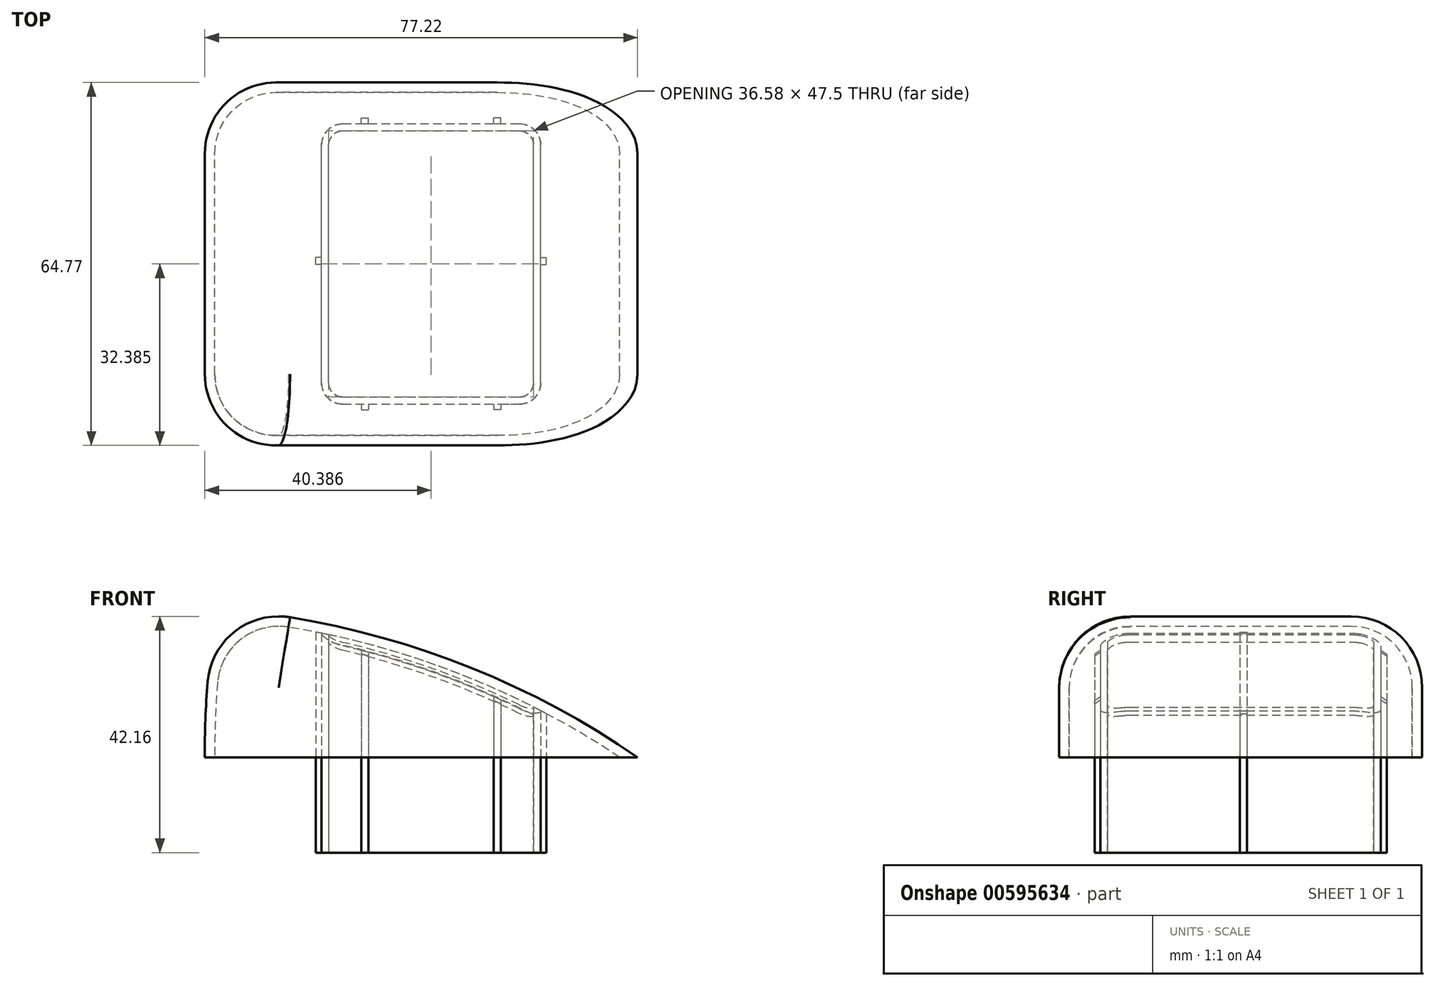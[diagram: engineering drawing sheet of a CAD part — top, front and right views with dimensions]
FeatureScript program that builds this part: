
annotation { "Feature Type Name" : "Feature", "Feature Type Description" : "" }
export const myFeature = defineFeature(function(context is Context, id is Id, definition is map)
    precondition{}
    {
        {
            var Q0;
            Q0=qCreatedBy(makeId("Front.planeOp"),FACE);
            var sketch = newSketch(context, id + "F0", { "sketchPlane" : qUnion([Q0])});
            skLineSegment(sketch, "E0", {"start": v(0, 0) * mm, "end": v(77.22, 0) * mm});
            skArc(sketch, "E1", {"start": v(77.22, 0) * mm, "mid": v(46.3, 16.45) * mm, "end": v(12.45, 25.4) * mm});
            skArc(sketch, "E2", {"start": v(0.76, 16.26) * mm, "mid": v(0.16, 8.14) * mm, "end": v(0, 0) * mm});
            skArc(sketch, "E3", {"start": v(12.45, 25.4) * mm, "mid": v(5.03, 22.84) * mm, "end": v(0.76, 16.26) * mm});
            skSolve(sketch);
        }
        {
            var Q0;
            Q0=makeQuery(id+"F0.imprint","IMPRINT",FACE,{"disambiguationData":[TD([[makeQuery(id+"F0.imprint","IMPRINT",EDGE,{"derivedFrom":sQuery(id+"F0.wireOp",EDGE,"E0")}),1.0]])]});
            extrude(context, id + "F1", {"entities" : qUnion([Q0]), "depth" : 64.77 * mm, "offsetDistance" : 25.4 * mm});
        }
        {
            var Q0;
            Q0=makeQuery(id+"F1.opExtrude","CAP_EDGE",EDGE,{"disambiguationData":[OSD([sQuery(id+"F0.wireOp",EDGE,"E1")])],"isStart":false});
            var Q1;
            Q1=makeQuery(id+"F1.opExtrude","CAP_EDGE",EDGE,{"disambiguationData":[OSD([sQuery(id+"F0.wireOp",EDGE,"E2")])],"isStart":true});
            fillet(context, id + "F2", {"entities" : qUnion([Q0, Q1]), "radius" : 12.7 * mm, "tangentPropagation" : true, "allowEdgeOverflow" : false});
        }
        {
            var Q0;
            Q0=makeQuery(id+"F2.opFillet","BLEND_EDGE",EDGE,{"blendedFrom":[makeQuery(id+"F1.opExtrude","CAP_EDGE",EDGE,{"disambiguationData":[OSD([sQuery(id+"F0.wireOp",EDGE,"E2")])],"isStart":true}),makeQuery(id+"F1.opExtrude","SWEPT_FACE",FACE,{"disambiguationData":[OSD([sQuery(id+"F0.wireOp",EDGE,"E3")])]})],"blendedInto":[makeQuery(id+"F1.opExtrude","SWEPT_FACE",FACE,{"disambiguationData":[OSD([sQuery(id+"F0.wireOp",EDGE,"E3")])]})]});
            var Q1;
            Q1=makeQuery(id+"F1.opExtrude","CAP_EDGE",EDGE,{"disambiguationData":[OSD([sQuery(id+"F0.wireOp",EDGE,"E1")])],"isStart":true});
            fillet(context, id + "F3", {"entities" : qUnion([Q0, Q1]), "radius" : 12.7 * mm, "tangentPropagation" : true, "allowEdgeOverflow" : false});
        }
        {
            var Q0;
            Q0=makeQuery(id+"F3.opFillet","BLEND_EDGE",EDGE,{"blendedFrom":[makeQuery(id+"F1.opExtrude","SWEPT_EDGE",EDGE,{"disambiguationData":[OSD([sQuery(id+"F0.wireOp",EDGE,"E2"),sQuery(id+"F0.wireOp",EDGE,"E3")])]}),makeQuery(id+"F2.opFillet","BLEND_FACE",FACE,{"disambiguationData":[OSD([sQuery(id+"F0.wireOp",EDGE,"E1")])]})],"blendedInto":[makeQuery(id+"F2.opFillet","BLEND_FACE",FACE,{"disambiguationData":[OSD([sQuery(id+"F0.wireOp",EDGE,"E1")])]})]});
            fillet(context, id + "F4", {"entities" : qUnion([Q0]), "radius" : 12.7 * mm, "tangentPropagation" : true, "allowEdgeOverflow" : false});
        }
        {
            var Q0;
            Q0=makeQuery(id+"F1.opExtrude","SWEPT_FACE",FACE,{"disambiguationData":[OSD([sQuery(id+"F0.wireOp",EDGE,"E0")])]});
            shell(context, id + "F5", {"entities" : qUnion([Q0]), "thickness" : 1.78 * mm});
        }
        {
            var Q0;
            Q0=makeQuery(id+"F1.opExtrude","SWEPT_FACE",FACE,{"disambiguationData":[OSD([sQuery(id+"F0.wireOp",EDGE,"E0")])]});
            cPlane(context, id + "F6", {"entities" : qUnion([Q0]), "cplaneType" : CPlaneType.OFFSET, "offset" : 0 * mm, "width" : 152.4 * mm, "height" : 152.4 * mm});
        }
        {
            var Q0;
            Q0=qCreatedBy(id+"F6.planeOp",FACE);
            var sketch = newSketch(context, id + "F7", { "sketchPlane" : qUnion([Q0])});
            skLineSegment(sketch, "E4.bottom", {"start": v(24.64, 57.4) * mm, "end": v(56.13, 57.4) * mm});
            skLineSegment(sketch, "E4.top", {"start": v(24.64, 7.37) * mm, "end": v(56.13, 7.37) * mm});
            skLineSegment(sketch, "E4.left", {"start": v(20.83, 53.6) * mm, "end": v(20.83, 11.18) * mm});
            skLineSegment(sketch, "E4.right", {"start": v(59.94, 53.6) * mm, "end": v(59.94, 11.18) * mm});
            skPoint(sketch, "E5.visualSharp", {"position": v(20.83, 57.4) * mm});
            skArc(sketch, "E5.filletArc", {"start": v(24.64, 57.4) * mm, "mid": v(21.94, 56.29) * mm, "end": v(20.83, 53.6) * mm});
            skPoint(sketch, "E6.visualSharp", {"position": v(20.83, 7.37) * mm});
            skArc(sketch, "E6.filletArc", {"start": v(20.83, 11.18) * mm, "mid": v(21.94, 8.48) * mm, "end": v(24.64, 7.37) * mm});
            skPoint(sketch, "E7.visualSharp", {"position": v(59.94, 7.37) * mm});
            skArc(sketch, "E7.filletArc", {"start": v(56.13, 7.37) * mm, "mid": v(58.83, 8.48) * mm, "end": v(59.94, 11.18) * mm});
            skPoint(sketch, "E8.visualSharp", {"position": v(59.94, 57.4) * mm});
            skArc(sketch, "E8.filletArc", {"start": v(59.94, 53.6) * mm, "mid": v(58.83, 56.29) * mm, "end": v(56.13, 57.4) * mm});
            skSolve(sketch);
        }
        {
            var Q0;
            Q0=makeQuery(id+"F7.imprint","IMPRINT",FACE,{"disambiguationData":[TD([[makeQuery(id+"F7.imprint","IMPRINT",EDGE,{"derivedFrom":sQuery(id+"F7.wireOp",EDGE,"E4.bottom")}),-1.0]])]});
            extrude(context, id + "F8", {"entities" : qUnion([Q0]), "endBound" : BoundingType.UP_TO_NEXT, "oppositeDirection" : true, "depth" : 25.4 * mm, "offsetDistance" : 25.4 * mm});
        }
        {
            var Q0;
            Q0=makeQuery(id+"F8.opExtrude","CAP_FACE",FACE,{"disambiguationData":[OSD([sQuery(id+"F7.wireOp",EDGE,"E4.bottom"),sQuery(id+"F7.wireOp",EDGE,"E4.top"),sQuery(id+"F7.wireOp",EDGE,"E4.left"),sQuery(id+"F7.wireOp",EDGE,"E4.right"),sQuery(id+"F7.wireOp",EDGE,"E5.filletArc"),sQuery(id+"F7.wireOp",EDGE,"E6.filletArc"),sQuery(id+"F7.wireOp",EDGE,"E7.filletArc"),sQuery(id+"F7.wireOp",EDGE,"E8.filletArc")])],"isStart":true});
            extrude(context, id + "F9", {"entities" : qUnion([Q0]), "operationType" : NewBodyOperationType.ADD, "depth" : 17.02 * mm, "offsetDistance" : 25.4 * mm});
        }
        {
            var Q0;
            Q0=makeQuery(id+"F9.opExtrude","CAP_FACE",FACE,{"disambiguationData":[OSD([sQuery(id+"F7.wireOp",EDGE,"E4.bottom"),sQuery(id+"F7.wireOp",EDGE,"E4.top"),sQuery(id+"F7.wireOp",EDGE,"E4.left"),sQuery(id+"F7.wireOp",EDGE,"E4.right"),sQuery(id+"F7.wireOp",EDGE,"E5.filletArc"),sQuery(id+"F7.wireOp",EDGE,"E6.filletArc"),sQuery(id+"F7.wireOp",EDGE,"E7.filletArc"),sQuery(id+"F7.wireOp",EDGE,"E8.filletArc")])],"isStart":false});
            shell(context, id + "F10", {"entities" : qUnion([Q0]), "thickness" : 1.27 * mm});
        }
        {
            var Q0;
            Q0=makeQuery(id+"F9.opExtrude","CAP_FACE",FACE,{"disambiguationData":[OSD([sQuery(id+"F7.wireOp",EDGE,"E4.bottom"),sQuery(id+"F7.wireOp",EDGE,"E4.top"),sQuery(id+"F7.wireOp",EDGE,"E4.left"),sQuery(id+"F7.wireOp",EDGE,"E4.right"),sQuery(id+"F7.wireOp",EDGE,"E5.filletArc"),sQuery(id+"F7.wireOp",EDGE,"E6.filletArc"),sQuery(id+"F7.wireOp",EDGE,"E7.filletArc"),sQuery(id+"F7.wireOp",EDGE,"E8.filletArc")])],"isStart":false});
            var sketch = newSketch(context, id + "F11", { "sketchPlane" : qUnion([Q0])});
            skLineSegment(sketch, "E9", {"start": v(20.83, 57.4) * mm, "end": v(27.94, 57.4) * mm});
            skLineSegment(sketch, "E10.bottom", {"start": v(27.94, 57.4) * mm, "end": v(29.22, 57.4) * mm});
            skLineSegment(sketch, "E10.top", {"start": v(27.94, 58.42) * mm, "end": v(29.22, 58.42) * mm});
            skLineSegment(sketch, "E10.left", {"start": v(27.94, 57.4) * mm, "end": v(27.94, 58.42) * mm});
            skLineSegment(sketch, "E10.right", {"start": v(29.22, 57.4) * mm, "end": v(29.22, 58.42) * mm});
            skLineSegment(sketch, "E11", {"start": v(59.94, 57.4) * mm, "end": v(52.84, 57.4) * mm});
            skLineSegment(sketch, "E12.bottom", {"start": v(52.84, 57.4) * mm, "end": v(51.58, 57.4) * mm});
            skLineSegment(sketch, "E12.top", {"start": v(52.84, 58.42) * mm, "end": v(51.58, 58.42) * mm});
            skLineSegment(sketch, "E12.left", {"start": v(52.84, 57.4) * mm, "end": v(52.84, 58.42) * mm});
            skLineSegment(sketch, "E12.right", {"start": v(51.58, 57.4) * mm, "end": v(51.58, 58.42) * mm});
            skSolve(sketch);
        }
        {
            var Q0;
            Q0=makeQuery(id+"F11.imprint","IMPRINT",FACE,{"disambiguationData":[TD([[makeQuery(id+"F11.imprint","IMPRINT",EDGE,{"derivedFrom":sQuery(id+"F11.wireOp",EDGE,"E12.bottom")}),1.0]])]});
            var Q1;
            {var subQ4=sQuery(id+"F11.wireOp",EDGE,"E10.bottom");Q1=makeQuery(id+"F11.imprint","IMPRINT",FACE,{"disambiguationData":[TD([[makeQuery(id+"F11.imprint","IMPRINT",EDGE,{"derivedFrom":subQ4}),-1.0]])]});}
            var Q2;
            Q2=makeQuery(id+"F11.imprint","IMPRINT",FACE,{"disambiguationData":[TD([[makeQuery(id+"F11.imprint","IMPRINT",EDGE,{"derivedFrom":sQuery(id+"F11.wireOp",EDGE,"E10.bottom")}),1.0]])]});
            extrude(context, id + "F12", {"entities" : qUnion([Q0, Q1, Q2]), "endBound" : BoundingType.UP_TO_NEXT, "oppositeDirection" : true, "depth" : 25.4 * mm, "offsetDistance" : 25.4 * mm});
        }
        {
            var Q0;
            Q0=makeQuery(id+"F9.opExtrude","CAP_FACE",FACE,{"disambiguationData":[OSD([sQuery(id+"F7.wireOp",EDGE,"E4.bottom"),sQuery(id+"F7.wireOp",EDGE,"E4.top"),sQuery(id+"F7.wireOp",EDGE,"E4.left"),sQuery(id+"F7.wireOp",EDGE,"E4.right"),sQuery(id+"F7.wireOp",EDGE,"E5.filletArc"),sQuery(id+"F7.wireOp",EDGE,"E6.filletArc"),sQuery(id+"F7.wireOp",EDGE,"E7.filletArc"),sQuery(id+"F7.wireOp",EDGE,"E8.filletArc")])],"isStart":false});
            var sketch = newSketch(context, id + "F13", { "sketchPlane" : qUnion([Q0])});
            skLineSegment(sketch, "E13.bottom", {"start": v(27.94, 7.37) * mm, "end": v(29.21, 7.37) * mm});
            skLineSegment(sketch, "E13.top", {"start": v(27.94, 6.34) * mm, "end": v(29.21, 6.34) * mm});
            skLineSegment(sketch, "E13.left", {"start": v(27.94, 7.37) * mm, "end": v(27.94, 6.34) * mm});
            skLineSegment(sketch, "E13.right", {"start": v(29.21, 7.37) * mm, "end": v(29.21, 6.34) * mm});
            skLineSegment(sketch, "E14.bottom", {"start": v(52.83, 7.37) * mm, "end": v(51.56, 7.37) * mm});
            skLineSegment(sketch, "E14.top", {"start": v(52.83, 6.34) * mm, "end": v(51.56, 6.34) * mm});
            skLineSegment(sketch, "E14.left", {"start": v(52.83, 7.37) * mm, "end": v(52.83, 6.34) * mm});
            skLineSegment(sketch, "E14.right", {"start": v(51.56, 7.37) * mm, "end": v(51.56, 6.34) * mm});
            skLineSegment(sketch, "E15", {"start": v(20.83, 57.4) * mm, "end": v(20.83, 32.51) * mm});
            skSolve(sketch);
        }
        {
            var Q0;
            Q0=makeQuery(id+"F13.imprint","IMPRINT",FACE,{"disambiguationData":[TD([[makeQuery(id+"F13.imprint","IMPRINT",EDGE,{"derivedFrom":sQuery(id+"F13.wireOp",EDGE,"E13.bottom")}),-1.0]])]});
            var Q1;
            Q1=makeQuery(id+"F13.imprint","IMPRINT",FACE,{"disambiguationData":[TD([[makeQuery(id+"F13.imprint","IMPRINT",EDGE,{"derivedFrom":sQuery(id+"F13.wireOp",EDGE,"E14.bottom")}),-1.0]])]});
            extrude(context, id + "F14", {"entities" : qUnion([Q0, Q1]), "endBound" : BoundingType.UP_TO_NEXT, "oppositeDirection" : true, "depth" : 25.4 * mm, "offsetDistance" : 25.4 * mm});
        }
        {
            var Q0;
            Q0=makeQuery(id+"F9.opExtrude","CAP_FACE",FACE,{"disambiguationData":[OSD([sQuery(id+"F7.wireOp",EDGE,"E4.bottom"),sQuery(id+"F7.wireOp",EDGE,"E4.top"),sQuery(id+"F7.wireOp",EDGE,"E4.left"),sQuery(id+"F7.wireOp",EDGE,"E4.right"),sQuery(id+"F7.wireOp",EDGE,"E5.filletArc"),sQuery(id+"F7.wireOp",EDGE,"E6.filletArc"),sQuery(id+"F7.wireOp",EDGE,"E7.filletArc"),sQuery(id+"F7.wireOp",EDGE,"E8.filletArc")])],"isStart":false});
            var sketch = newSketch(context, id + "F15", { "sketchPlane" : qUnion([Q0])});
            skLineSegment(sketch, "E16", {"start": v(20.83, 57.4) * mm, "end": v(20.83, 32.51) * mm});
            skLineSegment(sketch, "E17", {"start": v(59.94, 57.4) * mm, "end": v(59.94, 32.51) * mm});
            skLineSegment(sketch, "E18.bottom", {"start": v(59.94, 32.51) * mm, "end": v(60.96, 32.51) * mm});
            skLineSegment(sketch, "E18.top", {"start": v(59.94, 31.24) * mm, "end": v(60.96, 31.24) * mm});
            skLineSegment(sketch, "E18.left", {"start": v(59.94, 32.51) * mm, "end": v(59.94, 31.24) * mm});
            skLineSegment(sketch, "E18.right", {"start": v(60.96, 32.51) * mm, "end": v(60.96, 31.24) * mm});
            skLineSegment(sketch, "E19.bottom", {"start": v(20.83, 32.51) * mm, "end": v(19.81, 32.51) * mm});
            skLineSegment(sketch, "E19.top", {"start": v(20.83, 31.24) * mm, "end": v(19.81, 31.24) * mm});
            skLineSegment(sketch, "E19.left", {"start": v(20.83, 32.51) * mm, "end": v(20.83, 31.24) * mm});
            skLineSegment(sketch, "E19.right", {"start": v(19.81, 32.51) * mm, "end": v(19.81, 31.24) * mm});
            skSolve(sketch);
        }
        {
            var Q0;
            Q0=makeQuery(id+"F15.imprint","IMPRINT",FACE,{"disambiguationData":[TD([[makeQuery(id+"F15.imprint","IMPRINT",EDGE,{"derivedFrom":sQuery(id+"F15.wireOp",EDGE,"E19.bottom")}),1.0]])]});
            var Q1;
            Q1=makeQuery(id+"F15.imprint","IMPRINT",FACE,{"disambiguationData":[TD([[makeQuery(id+"F15.imprint","IMPRINT",EDGE,{"derivedFrom":sQuery(id+"F15.wireOp",EDGE,"E18.bottom")}),-1.0]])]});
            extrude(context, id + "F16", {"entities" : qUnion([Q0, Q1]), "endBound" : BoundingType.UP_TO_NEXT, "oppositeDirection" : true, "depth" : 25.4 * mm, "offsetDistance" : 25.4 * mm});
        }
    });
